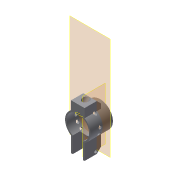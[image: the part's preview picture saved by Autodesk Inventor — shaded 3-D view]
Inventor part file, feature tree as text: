
AUTODESK INVENTOR PART (.ipt)
format: ipt  version: 2019.4 (Build 234330000, 330)  size: 290,304 bytes
history: native  units: mm
features: reference x12, extrude x9, sketch x9, other x6, plane x4, projected_geometry x3, pattern_circular x2, chamfer x1
ambient origin geometry x8: Origin, YZ Plane, XZ Plane, XY Plane, X Axis, Y Axis, Z Axis, Center Point
bodies: Solid1 (feature_tree)
feature tree (46):
  plane  "Work Plane1"
  extrude  "Extrusion1"  Depth=25.0mm
  extrude  "Extrusion3"  Depth=10.0mm TaperAngle=0.0deg
  plane  "Work Plane2"
  plane  "Work Plane3"
  extrude  "Extrusion4"  Depth=10.0mm
  extrude  "Extrusion5"  Depth=10.0mm TaperAngle=45.0deg
  chamfer  "Chamfer1"  Distance=10.0mm
  extrude  "Extrusion6"  Depth=10.0mm TaperAngle=0.0deg
  extrude  "Extrusion7"  Depth=20.0mm
  pattern_circular  "Circular Pattern1"  [2 undecoded]
  pattern_circular  "Circular Pattern2"  [2 undecoded]
  plane  "Work Plane4"
  extrude  "Extrusion8"  TaperAngle=0.0deg  [1 undecoded]
  extrude  "Extrusion9"  Depth=3.0mm TaperAngle=0.0deg
  extrude  "Extrusion10"  [1 undecoded]
  sketch  "Sketch1"  dims[d0=22.2mm d1=25.0mm]
  reference  "Reference1"
  sketch  "Sketch2"  dims[d2=10.0mm d3=0.0mm d7=12.0mm d8=0.0mm]
  reference  "Reference2"
  reference  "Reference3"
  reference  "Reference4"
  sketch  "Sketch3"  dims[d9=10.0mm d10=0.0mm d11=6.3mm]
  reference  "Reference5"
  sketch  "Sketch4"  dims[d12=10.0mm d13=0.0mm d14=4.0mm d15=2.0mm d16=45.0deg]
  reference  "Reference6"
  reference  "Reference7"
  reference  "Reference8"
  reference  "Reference9"
  sketch  "Sketch5"  dims[d17=2.9mm d18=10.0mm d19=0.0mm]
  projected_geometry  "Projected Loop1"
  sketch  "Sketch6"  dims[d20=2.9mm d21=10.0mm d22=0.0mm]
  reference  "Reference10"
  reference  "Reference11"
  sketch  "Sketch7"  dims[d23=20.0mm d24=30.0deg d26=20.0mm d27=-5.235988mm]
  projected_geometry  "Projected Loop2"
  reference  "Reference12"
  sketch  "Sketch8"  dims[d29=2.9mm]
  sketch  "Sketch9"  dims[d30=4.0mm d31=0.0mm d32=13.0mm d33=3.0mm d34=0.0mm d35=0.0mm d36=0.0mm d37=3.0mm d38=0.0mm]
  projected_geometry  "Projected Loop3"
  other  "Assembly_Autofocus_10x_laser_espcam_v1.iam"
  other  "00_objectivelens_10x:1"
  other  "00_IR_Laserdiode:1"
  other  "00_ESP32_Camera_only:1"
  other  "Assembly_Opentrons_Autofocus_v1.iam"
  other  "00_opticalpath:1"
note: 6 required parameter values undecoded (feature->parameter linkage not recoverable at this tier; creation-order binding heuristic only, values carry confidence <= 0.55)
